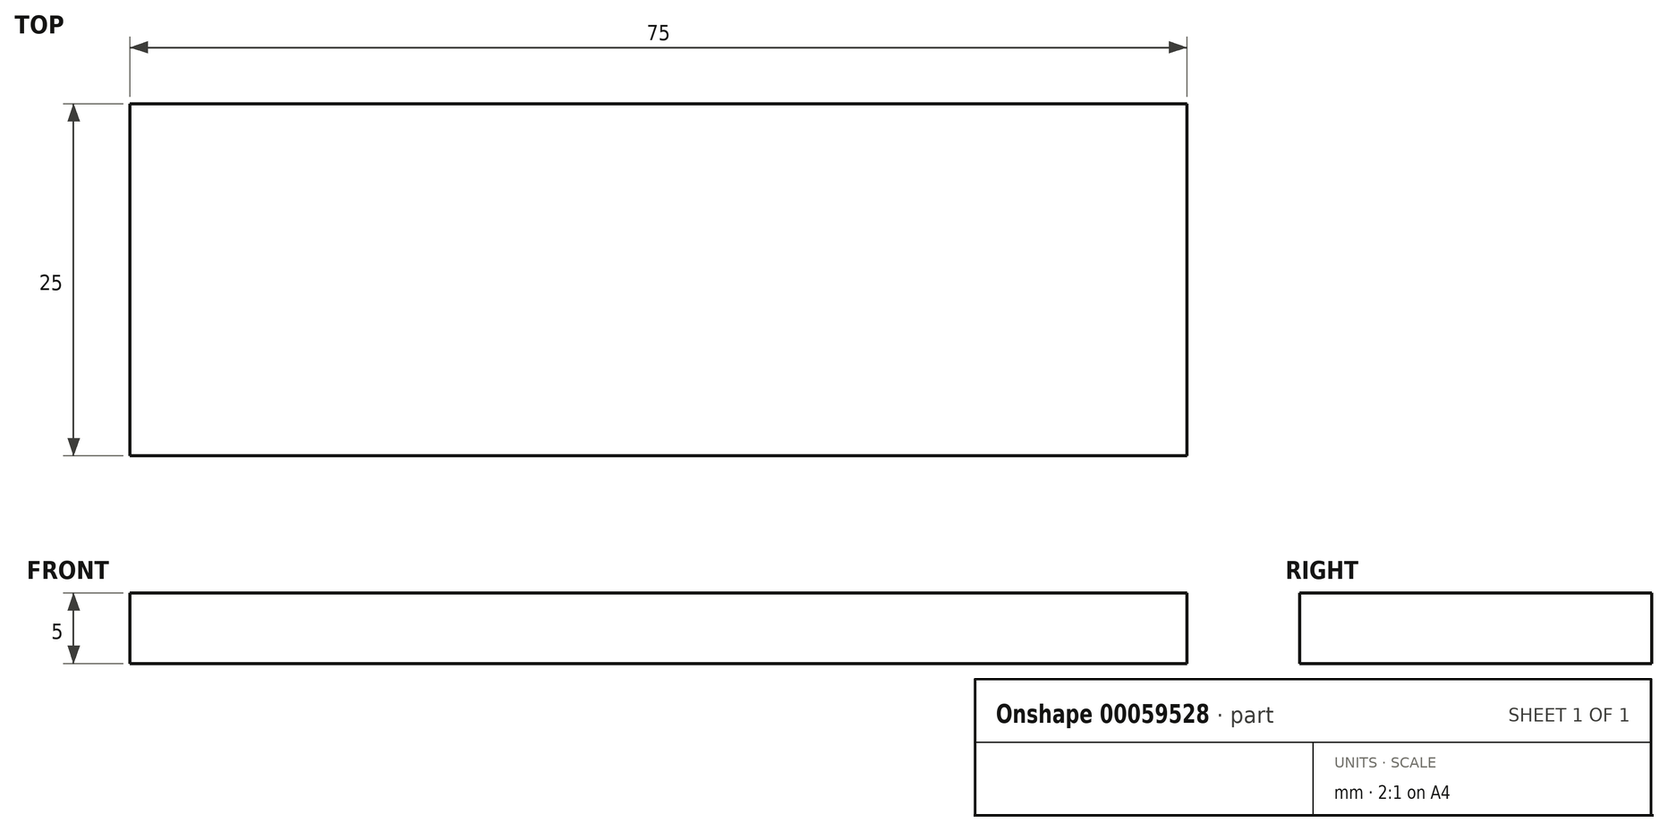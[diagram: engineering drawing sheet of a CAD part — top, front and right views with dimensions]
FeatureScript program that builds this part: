
annotation { "Feature Type Name" : "Feature", "Feature Type Description" : "" }
export const myFeature = defineFeature(function(context is Context, id is Id, definition is map)
    precondition{}
    {
        {
            var Q0;
            Q0=qCreatedBy(makeId("Top.planeOp"),FACE);
            var sketch = newSketch(context, id + "F0", { "sketchPlane" : qUnion([Q0])});
            skLineSegment(sketch, "E0.bottom", {"start": v(-37.5, 12.5) * mm, "end": v(37.5, 12.5) * mm});
            skLineSegment(sketch, "E0.top", {"start": v(-37.5, -12.5) * mm, "end": v(37.5, -12.5) * mm});
            skLineSegment(sketch, "E0.left", {"start": v(-37.5, 12.5) * mm, "end": v(-37.5, -12.5) * mm});
            skLineSegment(sketch, "E0.right", {"start": v(37.5, 12.5) * mm, "end": v(37.5, -12.5) * mm});
            skSolve(sketch);
        }
        {
            var Q0;
            Q0 = qSketchRegion(id + "F0", true);
            extrude(context, id + "F1", {"entities" : qUnion([Q0]), "depth" : 5 * mm});
        }
    });
